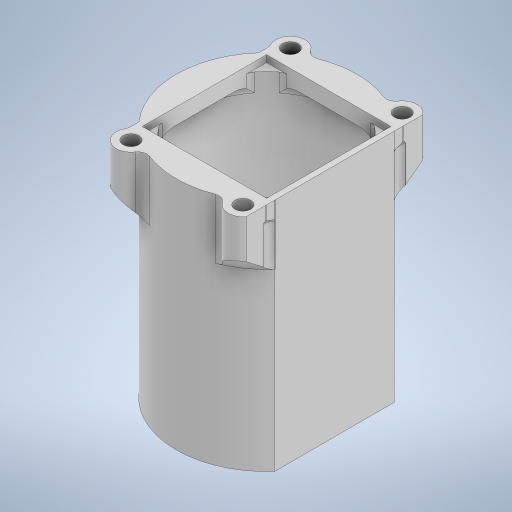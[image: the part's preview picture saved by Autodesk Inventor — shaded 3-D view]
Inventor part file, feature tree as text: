
AUTODESK INVENTOR PART (.ipt)
format: ipt  version: 2024 (Build 280153000, 153)  size: 602,624 bytes
history: native  units: in
note: dims shown in document units (in); Inventor stores cm internally (conversion verified against a paired STEP export)
features: extrude x12, projected_geometry x7, sketch x6, fillet x4, chamfer x1
ambient origin geometry x8: Origin, YZ Plane, XZ Plane, XY Plane, X Axis, Y Axis, Z Axis, Center Point
bodies: Solid1 (feature_tree)
feature tree (30):
  extrude  "Extrusion1"  Depth=1.5748in
  extrude  "Extrusion2"  Depth=1.0236in
  extrude  "Extrusion3"  Depth=0.1181in
  sketch  "Sketch4"  dims[d8=1.7106in d9=0.0in d10=0.1378in]
  extrude  "Extrusion4"  Depth=0.1378in
  extrude  "Extrusion5"  Depth=0.9744in
  extrude  "Extrusion6"  Depth=0.4872in
  extrude  "Extrusion7"  Depth=0.6939in
  extrude  "Extrusion8"  Depth=0.2559in
  fillet  "Fillet1"  Radius=1.1811in
  extrude  "Extrusion9"  Depth=0.5906in
  chamfer  "Chamfer1"  Distance=0.5906in
  fillet  "Fillet4"  Radius=0.2362in
  fillet  "Fillet5"  Radius=0.2362in
  fillet  "Fillet6"  Radius=0.0492in
  extrude  "Extrusion10"  Depth=1.3878in
  extrude  "Extrusion11"  Depth=0.0787in TaperAngle=0.0deg
  extrude  "Extrusion12"  Depth=0.0591in TaperAngle=0.0deg
  sketch  "Sketch1"  dims[d0=0.878in d1=1.5748in]
  sketch  "Sketch2"  dims[d2=0.1181in d3=0.0in d4=1.0236in]
  sketch  "Sketch3"  dims[d5=0.1575in d6=0.0in d7=0.1181in]
  projected_geometry  "Projected Loop1"
  projected_geometry  "Projected Loop2"
  sketch  "Sketch5"  dims[d14=1.3878in d15=0.9744in]
  projected_geometry  "Projected Loop3"
  projected_geometry  "Projected Loop4"
  projected_geometry  "Projected Loop5"
  projected_geometry  "Projected Loop6"
  sketch  "Sketch6"  dims[d17=0.9744in d18=0.4872in d19=0.6939in d20=0.2559in d21=1.1811in d22=0.5906in d23=0.5906in d25=0.2362in d26=0.0in d27=0.2362in d28=0.0in d29=0.0492in d30=1.3878in d31=0.0787in d32=0.0in d33=0.0591in d34=0.0in d35=0.0591in d36=0.0in d37=0.0787in d39=0.0394in d40=0.0in d42=0.187in d43=0.0787in d44=45.0deg d45=0.0197in d46=0.0787in d47=0.0787in d48=0.1181in d49=0.0in d50=1.9685in d51=0.0in d52=1.7717in d53=1.9685in d54=0.0in d41=0.0in]
  projected_geometry  "Projected Loop7"
